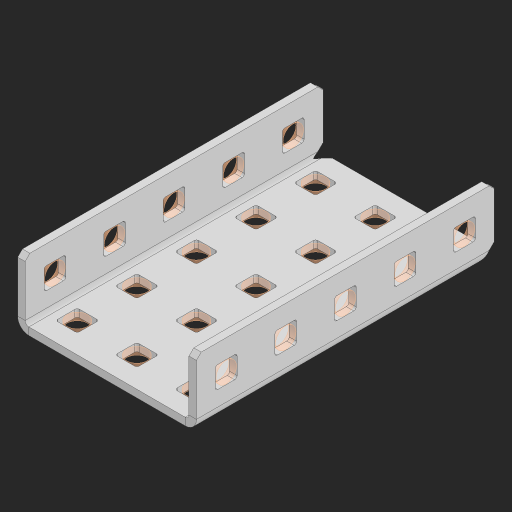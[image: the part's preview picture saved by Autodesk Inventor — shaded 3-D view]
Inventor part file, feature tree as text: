
AUTODESK INVENTOR PART (.ipt)
format: ipt  version: 2023 (Build 270158000, 158)  size: 535,552 bytes
history: native  units: in
note: dims shown in document units (in); Inventor stores cm internally (conversion verified against a paired STEP export)
features: other x30, extrude x24, sheet_metal_op x10, sketch x8, mirror x1, pattern_linear x1, chamfer x1
ambient origin geometry x8: Origin, YZ Plane, XZ Plane, XY Plane, X Axis, Y Axis, Z Axis, Center Point
bodies: Solid1 (feature_tree), Body (feature_tree)
feature tree (75):
  other  "Flange Pattern Plane"
  sheet_metal_op  "Flange Pattern"
  sheet_metal_op  "Body Pattern"
  other  "Arc Length"
  mirror  "Notch Mirror"
  pattern_linear  "Notch Pattern"  Spacing1=0.25in  [1 undecoded]
  chamfer  "End Chamfer"
  extrude  "Half Cut"  Depth=0.0625in
  sketch  "Sketch1"  dims[d0=1.5in]
  other  "Plate1"
  sketch  "Sketch2"  dims[d1=2.5in]
  other  "Plate2"
  sheet_metal_op  "Bend1"
  sheet_metal_op  "Corner1"
  sketch  "Sketch3"  dims[d2=0.0625in]
  other  "Flange Pattern Sketch"
  sketch  "Sketch7"  dims[d3=0.0625in]
  other  "Srf1"
  other  "Srf2"
  sketch  "Sketch8"  dims[d4=0.0312in]
  sketch  "Sketch9"  dims[d5=0.125in]
  other  "Srf91"
  sheet_metal_op  "Body Pattern Sketch"
  other  "Srf92"
  sketch  "Sketch13"  dims[d6=0.0625in]
  sketch  "Sketch14"  dims[d7=0.5in d8=90.0deg d9=0.0312in d10=0.25in d11=0.0625in d12=0.0625in d16=0.182in d17=0.02in d18=0.0625in d19=0.0in d20=0.25in d21=0.25in d46=0.172in d47=1.0in d48=0.0in d49=0.182in d50=0.02in d51=0.25in d52=0.25in d53=0.0625in d54=0.0in d55=0.172in d56=1.0in d57=0.0in d60=1.9685in d62=0.5in d63=1.1811in d65=0.5in d85=0.1473in d86=0.1782in d88=0.04in d89=0.0625in d90=0.0in d91=0.04in d92=0.0491in d95=2.5in d96=0.04in d97=0.25in d98=45.0deg d101=0.0in d102=2.497in d131=1.5in d132=1.9685in d134=0.5in d139=0.5in]
  other  "Srf856"
  other  "Srf1310"
  other  "Srf1311"
  other  "Srf1312"
  other  "Srf1376"
  other  "Srf1377"
  other  "Srf1728"
  other  "Srf1755"
  other  "Srf1878"
  other  "Srf1879"
  other  "Srf1880"
  other  "Srf1881"
  other  "Srf1942"
  other  "Srf1943"
  other  "Srf1944"
  other  "Srf1945"
  other  "Srf1946"
  other  "Srf1947"
  other  "Srf1948"
  other  "Srf1949"
  other  "Srf1950"
  sheet_metal_op  "Flange Stamp"
  sheet_metal_op  "Flange Circle"
  sheet_metal_op  "Body Stamp"
  sheet_metal_op  "Body Circle"
  sheet_metal_op  "Notch"
  extrude  "ExtrusionSrf2"  Depth=0.0625in
  extrude  "ExtrusionSrf92"  Depth=1.5in
  extrude  "ExtrusionSrf856"  Depth=0.02in
  extrude  "ExtrusionSrf1310"  Depth=0.0625in
  extrude  "ExtrusionSrf1311"  TaperAngle=0.0deg  [1 undecoded]
  extrude  "ExtrusionSrf1312"  Depth=0.25in
  extrude  "ExtrusionSrf1376"  Depth=0.25in
  extrude  "ExtrusionSrf1377"  Depth=1.5in
  extrude  "ExtrusionSrf1728"  Depth=1.5in TaperAngle=0.0deg
  extrude  "ExtrusionSrf1755"  Depth=1.5in
  extrude  "ExtrusionSrf1878"  Depth=0.02in
  extrude  "ExtrusionSrf1879"  Depth=0.25in
  extrude  "ExtrusionSrf1880"  Depth=0.25in
  extrude  "ExtrusionSrf1881"  Depth=0.0625in
  extrude  "ExtrusionSrf1942"  TaperAngle=0.0deg  [1 undecoded]
  extrude  "ExtrusionSrf1943"  Depth=1.5in
  extrude  "ExtrusionSrf1944"  Depth=1.5in TaperAngle=0.0deg
  extrude  "ExtrusionSrf1945"  Depth=1.5in
  extrude  "ExtrusionSrf1946"  Depth=1.5in
  extrude  "ExtrusionSrf1947"  Depth=1.5in
  extrude  "ExtrusionSrf1948"  Depth=1.5in
  extrude  "ExtrusionSrf1949"  Depth=1.5in
  extrude  "ExtrusionSrf1950"  Depth=0.0625in
note: 3 required parameter values undecoded (feature->parameter linkage not recoverable at this tier; creation-order binding heuristic only, values carry confidence <= 0.55)
